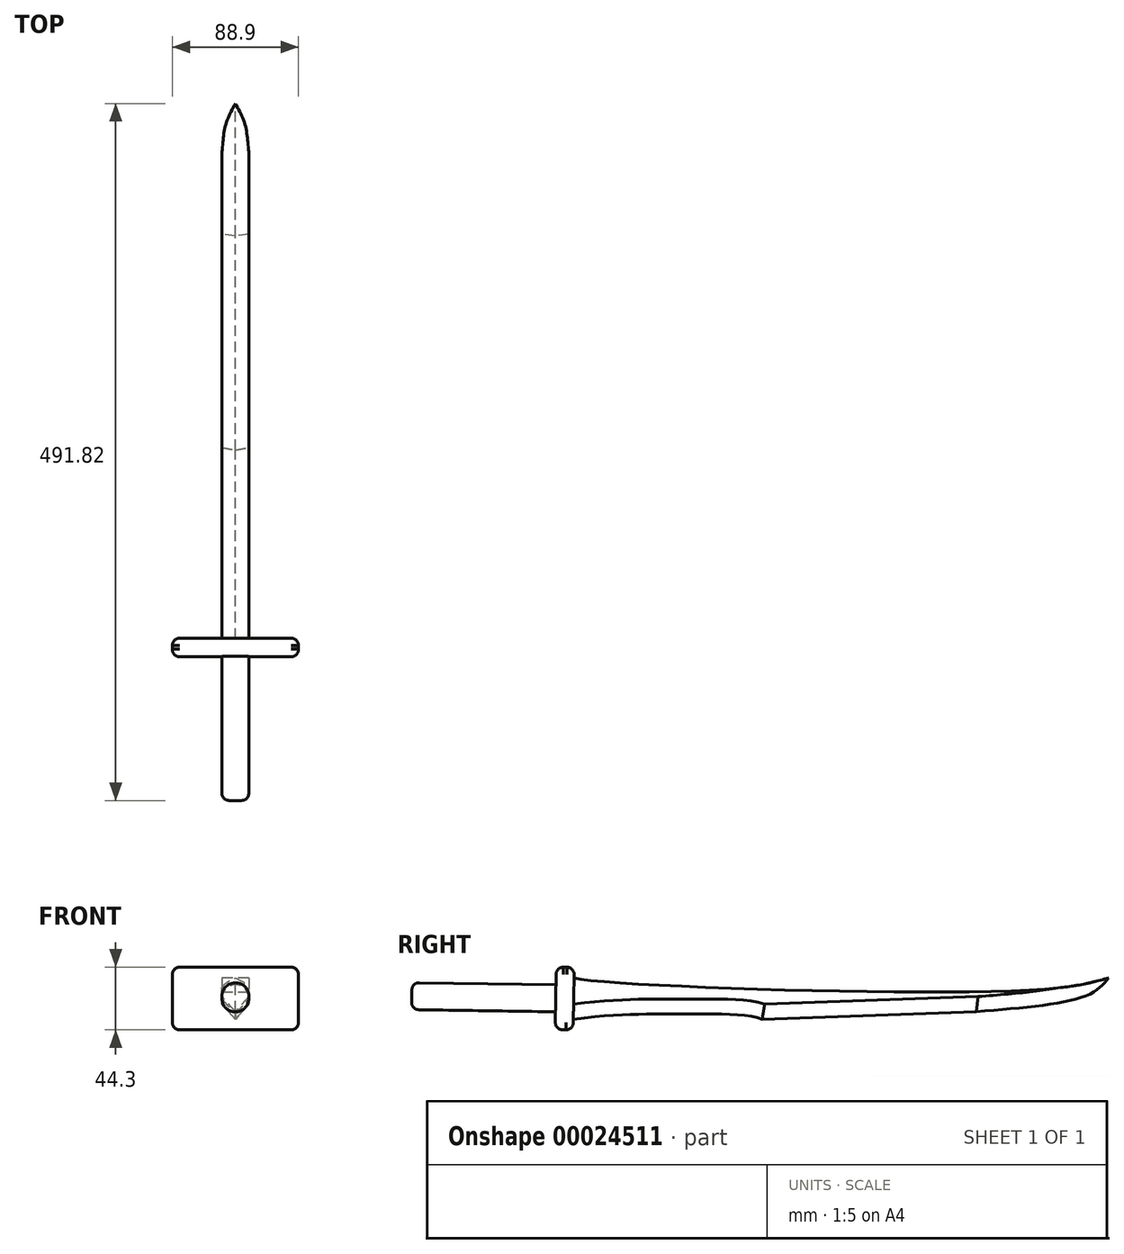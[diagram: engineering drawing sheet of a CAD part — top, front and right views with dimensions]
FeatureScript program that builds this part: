
annotation { "Feature Type Name" : "Feature", "Feature Type Description" : "" }
export const myFeature = defineFeature(function(context is Context, id is Id, definition is map)
    precondition{}
    {
        {
            var Q0;
            Q0=qCreatedBy(makeId("Right.planeOp"),FACE);
            var sketch = newSketch(context, id + "F0", { "sketchPlane" : qUnion([Q0])});
            skFitSpline(sketch, "E0", {"points": [v(0, 0) * mm, v(-14.62, -11.92) * mm, v(-93.35, -23.62) * mm], "startDerivative": vector(-32.8, -39.52) * mm, "endDerivative": vector(-141.4, -11) * mm});
            skLineSegment(sketch, "E1", {"start": v(-93.35, -23.62) * mm, "end": v(-244.5, -29.02) * mm});
            skFitSpline(sketch, "E2", {"points": [v(-244.5, -29.02) * mm, v(-301.66, -25.42) * mm, v(-377.69, -29.02) * mm], "startDerivative": vector(-70.94, 29.22) * mm, "endDerivative": vector(-184.3, -23.99) * mm});
            skFitSpline(sketch, "E3", {"points": [v(-377.24, 0) * mm, v(-52.88, -8.32) * mm, v(0, 0) * mm], "startDerivative": vector(106.12, -24.96) * mm, "endDerivative": vector(105.82, 24.98) * mm});
            skLineSegment(sketch, "E4", {"start": v(-377.24, 0) * mm, "end": v(-377.69, -29.02) * mm});
            skSolve(sketch);
        }
        {
            var Q0;
            Q0 = qSketchRegion(id + "F0", true);
            extrude(context, id + "F1", {"entities" : qUnion([Q0]), "depth" : 19.05 * mm});
        }
        {
            var Q0;
            Q0=makeQuery(id+"F1.opExtrude","SWEPT_FACE",FACE,{"disambiguationData":[OSD([sQuery(id+"F0.wireOp",EDGE,"E4")])]});
            var sketch = newSketch(context, id + "F2", { "sketchPlane" : qUnion([Q0])});
            skLineSegment(sketch, "E5", {"start": v(9.53, -34.87) * mm, "end": v(0, -24.2) * mm});
            skLineSegment(sketch, "E6", {"start": v(19.05, -24.2) * mm, "end": v(9.53, -34.87) * mm});
            skSolve(sketch);
        }
        {
            var Q0;
            {var subQ2=sQuery(id+"F2.wireOp",EDGE,"E5");Q0=makeQuery(id+"F2.imprint","IMPRINT",FACE,{"disambiguationData":[TD([[makeQuery(id+"F2.imprint","IMPRINT",EDGE,{"derivedFrom":subQ2}),1.0]])]});}
            var Q1;
            {var subQ2=sQuery(id+"F2.wireOp",EDGE,"E6");Q1=makeQuery(id+"F2.imprint","IMPRINT",FACE,{"disambiguationData":[TD([[makeQuery(id+"F2.imprint","IMPRINT",EDGE,{"derivedFrom":subQ2}),1.0]])]});}
            var Q2;
            Q2=makeQuery(id+"F1.opExtrude","CAP_EDGE",EDGE,{"disambiguationData":[OSD([sQuery(id+"F0.wireOp",EDGE,"E2")])],"isStart":false});
            var Q3;
            Q3=makeQuery(id+"F1.opExtrude","CAP_EDGE",EDGE,{"disambiguationData":[OSD([sQuery(id+"F0.wireOp",EDGE,"E1")])],"isStart":false});
            sweep(context, id + "F3", {"operationType" : NewBodyOperationType.REMOVE, "profiles" : qUnion([Q0, Q1]), "path" : qUnion([Q2, Q3])});
        }
        {
            var Q0;
            Q0=makeQuery(id+"F3.boolean.opBoolean","COPY",FACE,{"derivedFrom":makeQuery(id+"F3.opSweep","CAP_FACE",FACE,{"disambiguationData":[OSD([sQuery(id+"F0.wireOp",EDGE,"E0"),sQuery(id+"F0.wireOp",EDGE,"E1"),sQuery(id+"F0.wireOp",EDGE,"E2"),sQuery(id+"F0.wireOp",EDGE,"E4"),sQuery(id+"F2.wireOp",EDGE,"E6")])],"isStart":false})});
            var Q1;
            Q1=makeQuery(id+"F3.boolean.opBoolean","COPY",FACE,{"derivedFrom":makeQuery(id+"F3.opSweep","CAP_FACE",FACE,{"disambiguationData":[OSD([sQuery(id+"F0.wireOp",EDGE,"E0"),sQuery(id+"F0.wireOp",EDGE,"E1"),sQuery(id+"F0.wireOp",EDGE,"E2"),sQuery(id+"F0.wireOp",EDGE,"E4"),sQuery(id+"F2.wireOp",EDGE,"E5")])],"isStart":false})});
            var Q2;
            Q2=makeQuery(id+"F1.opExtrude","CAP_EDGE",EDGE,{"disambiguationData":[OSD([sQuery(id+"F0.wireOp",EDGE,"E0")])],"isStart":true});
            sweep(context, id + "F4", {"operationType" : NewBodyOperationType.REMOVE, "profiles" : qUnion([Q0, Q1]), "path" : qUnion([Q2])});
        }
        {
            var Q0;
            Q0=makeQuery(id+"F1.opExtrude","SWEPT_FACE",FACE,{"disambiguationData":[OSD([sQuery(id+"F0.wireOp",EDGE,"E4")])]});
            var sketch = newSketch(context, id + "F5", { "sketchPlane" : qUnion([Q0])});
            skLineSegment(sketch, "E7", {"start": v(9.53, -34.87) * mm, "end": v(28.58, -34.87) * mm});
            skLineSegment(sketch, "E8", {"start": v(9.53, -34.87) * mm, "end": v(-9.52, -34.87) * mm});
            skLineSegment(sketch, "E9", {"start": v(9.53, -5.85) * mm, "end": v(28.58, -5.85) * mm});
            skLineSegment(sketch, "E10", {"start": v(9.53, -5.85) * mm, "end": v(-9.52, -5.85) * mm});
            skLineSegment(sketch, "E11", {"start": v(-9.52, -5.85) * mm, "end": v(-9.52, -34.87) * mm});
            skLineSegment(sketch, "E12", {"start": v(28.58, -5.85) * mm, "end": v(28.58, -34.87) * mm});
            skSolve(sketch);
        }
        {
            var Q0;
            Q0 = qSketchRegion(id + "F5", true);
            extrude(context, id + "F6", {"entities" : qUnion([Q0]), "operationType" : NewBodyOperationType.ADD, "depth" : 12.7 * mm});
        }
        {
            var Q0;
            Q0=makeQuery(id+"F6.opExtrude","SWEPT_FACE",FACE,{"disambiguationData":[OSD([sQuery(id+"F5.wireOp",EDGE,"E11")])]});
            extrude(context, id + "F7", {"entities" : qUnion([Q0]), "operationType" : NewBodyOperationType.ADD, "depth" : 25.4 * mm});
        }
        {
            var Q0;
            Q0=makeQuery(id+"F6.opExtrude","SWEPT_FACE",FACE,{"disambiguationData":[OSD([sQuery(id+"F5.wireOp",EDGE,"E12")])]});
            extrude(context, id + "F8", {"entities" : qUnion([Q0]), "operationType" : NewBodyOperationType.ADD, "depth" : 25.4 * mm});
        }
        {
            var Q0;
            {var subQ0=sQuery(id+"F5.wireOp",EDGE,"E9");var subQ1=sQuery(id+"F5.wireOp",EDGE,"E10");Q0=makeQuery(id+"F8.boolean.opBoolean","MERGE",FACE,{"derivedFrom":[makeQuery(id+"F7.boolean.opBoolean","MERGE",FACE,{"derivedFrom":[makeQuery(id+"F6.opExtrude","SWEPT_FACE",FACE,{"disambiguationData":[OSD([subQ0,subQ1])]}),makeQuery(id+"F7.opExtrude","SWEPT_FACE",FACE,{"disambiguationData":[OSD([subQ1,sQuery(id+"F5.wireOp",EDGE,"E11")])]})]}),makeQuery(id+"F8.opExtrude","SWEPT_FACE",FACE,{"disambiguationData":[OSD([subQ0,sQuery(id+"F5.wireOp",EDGE,"E12")])]})]});}
            extrude(context, id + "F9", {"entities" : qUnion([Q0]), "operationType" : NewBodyOperationType.ADD, "depth" : 7.62 * mm});
        }
        {
            var Q0;
            {var subQ0=sQuery(id+"F5.wireOp",EDGE,"E7");var subQ1=sQuery(id+"F5.wireOp",EDGE,"E8");Q0=makeQuery(id+"F8.boolean.opBoolean","MERGE",FACE,{"derivedFrom":[makeQuery(id+"F7.boolean.opBoolean","MERGE",FACE,{"derivedFrom":[makeQuery(id+"F6.opExtrude","SWEPT_FACE",FACE,{"disambiguationData":[OSD([subQ0,subQ1])]}),makeQuery(id+"F7.opExtrude","SWEPT_FACE",FACE,{"disambiguationData":[OSD([subQ1,sQuery(id+"F5.wireOp",EDGE,"E11")])]})]}),makeQuery(id+"F8.opExtrude","SWEPT_FACE",FACE,{"disambiguationData":[OSD([subQ0,sQuery(id+"F5.wireOp",EDGE,"E12")])]})]});}
            extrude(context, id + "F10", {"entities" : qUnion([Q0]), "operationType" : NewBodyOperationType.ADD, "depth" : 7.62 * mm});
        }
        {
            var Q0;
            {var subQ0=sQuery(id+"F5.wireOp",EDGE,"E7");var subQ1=sQuery(id+"F5.wireOp",EDGE,"E8");var subQ2=sQuery(id+"F5.wireOp",EDGE,"E9");var subQ3=sQuery(id+"F5.wireOp",EDGE,"E10");var subQ4=sQuery(id+"F5.wireOp",EDGE,"E11");var subQ5=sQuery(id+"F5.wireOp",EDGE,"E12");Q0=makeQuery(id+"F10.boolean.opBoolean","MERGE",FACE,{"derivedFrom":[makeQuery(id+"F9.boolean.opBoolean","MERGE",FACE,{"derivedFrom":[makeQuery(id+"F8.boolean.opBoolean","MERGE",FACE,{"derivedFrom":[makeQuery(id+"F7.boolean.opBoolean","MERGE",FACE,{"derivedFrom":[makeQuery(id+"F6.opExtrude","CAP_FACE",FACE,{"disambiguationData":[OSD([subQ0,subQ1,subQ2,subQ3,subQ4,subQ5])],"isStart":false}),makeQuery(id+"F7.opExtrude","SWEPT_FACE",FACE,{"disambiguationData":[OSD([subQ4]),TDD([makeQuery(id+"F6.opExtrude","CAP_EDGE",EDGE,{"disambiguationData":[OSD([subQ4])],"isStart":false})])]})]}),makeQuery(id+"F8.opExtrude","SWEPT_FACE",FACE,{"disambiguationData":[OSD([subQ5]),TDD([makeQuery(id+"F6.opExtrude","CAP_EDGE",EDGE,{"disambiguationData":[OSD([subQ5])],"isStart":false})])]})]}),makeQuery(id+"F9.opExtrude","SWEPT_FACE",FACE,{"disambiguationData":[OSD([subQ2,subQ3,subQ4,subQ5])]})]}),makeQuery(id+"F10.opExtrude","SWEPT_FACE",FACE,{"disambiguationData":[OSD([subQ0,subQ1,subQ4,subQ5]),TDD([makeQuery(id+"F8.boolean.opBoolean","MERGE",EDGE,{"derivedFrom":[makeQuery(id+"F7.boolean.opBoolean","MERGE",EDGE,{"derivedFrom":[makeQuery(id+"F6.opExtrude","CAP_EDGE",EDGE,{"disambiguationData":[OSD([subQ0,subQ1])],"isStart":false}),makeQuery(id+"F7.opExtrude","SWEPT_EDGE",EDGE,{"disambiguationData":[OSD([subQ1,subQ4]),TDD([makeQuery(id+"F6.opExtrude","CAP_VERTEX",VERTEX,{"disambiguationData":[OSD([subQ1,subQ4])],"isStart":false})])]})]}),makeQuery(id+"F8.opExtrude","SWEPT_EDGE",EDGE,{"disambiguationData":[OSD([subQ0,subQ5]),TDD([makeQuery(id+"F6.opExtrude","CAP_VERTEX",VERTEX,{"disambiguationData":[OSD([subQ0,subQ5])],"isStart":false})])]})]})])]})]});}
            var sketch = newSketch(context, id + "F11", { "sketchPlane" : qUnion([Q0])});
            skCircle(sketch, "E13", {"center": v(9.53, -20.36) * mm, "radius": 9.53 * mm});
            skSolve(sketch);
        }
        {
            var Q0;
            Q0=makeQuery(id+"F9.opExtrude","CAP_EDGE",EDGE,{"disambiguationData":[OSD([sQuery(id+"F5.wireOp",EDGE,"E9"),sQuery(id+"F5.wireOp",EDGE,"E10"),sQuery(id+"F5.wireOp",EDGE,"E11"),sQuery(id+"F5.wireOp",EDGE,"E12")])],"isStart":false});
            var Q1;
            Q1=makeQuery(id+"F9.opExtrude","CAP_EDGE",EDGE,{"disambiguationData":[OSD([sQuery(id+"F0.wireOp",EDGE,"E3"),sQuery(id+"F0.wireOp",EDGE,"E4"),sQuery(id+"F5.wireOp",EDGE,"E9"),sQuery(id+"F5.wireOp",EDGE,"E10"),sQuery(id+"F5.wireOp",EDGE,"E11"),sQuery(id+"F5.wireOp",EDGE,"E12")])],"isStart":false});
            var Q2;
            {var subQ0=sQuery(id+"F5.wireOp",EDGE,"E11");var subQ1=sQuery(id+"F5.wireOp",EDGE,"E10");var subQ2=sQuery(id+"F5.wireOp",EDGE,"E8");Q2=makeQuery(id+"F10.boolean.opBoolean","MERGE",EDGE,{"derivedFrom":[makeQuery(id+"F9.boolean.opBoolean","MERGE",EDGE,{"derivedFrom":[makeQuery(id+"F7.opExtrude","CAP_EDGE",EDGE,{"disambiguationData":[OSD([subQ0]),TDD([makeQuery(id+"F6.opExtrude","CAP_EDGE",EDGE,{"disambiguationData":[OSD([subQ0])],"isStart":true})])],"isStart":false}),makeQuery(id+"F9.opExtrude","SWEPT_EDGE",EDGE,{"disambiguationData":[OSD([subQ1,subQ0]),TDD([makeQuery(id+"F7.opExtrude","CAP_VERTEX",VERTEX,{"disambiguationData":[OSD([subQ1,subQ0]),TDD([makeQuery(id+"F6.opExtrude","CAP_VERTEX",VERTEX,{"disambiguationData":[OSD([subQ1,subQ0])],"isStart":true})])],"isStart":false})])]})]}),makeQuery(id+"F10.opExtrude","SWEPT_EDGE",EDGE,{"disambiguationData":[OSD([subQ2,subQ0]),TDD([makeQuery(id+"F7.opExtrude","CAP_VERTEX",VERTEX,{"disambiguationData":[OSD([subQ2,subQ0]),TDD([makeQuery(id+"F6.opExtrude","CAP_VERTEX",VERTEX,{"disambiguationData":[OSD([subQ2,subQ0])],"isStart":true})])],"isStart":false})])]})]});}
            var Q3;
            {var subQ0=sQuery(id+"F5.wireOp",EDGE,"E11");var subQ1=sQuery(id+"F5.wireOp",EDGE,"E10");var subQ2=sQuery(id+"F5.wireOp",EDGE,"E8");Q3=makeQuery(id+"F10.boolean.opBoolean","MERGE",EDGE,{"derivedFrom":[makeQuery(id+"F9.boolean.opBoolean","MERGE",EDGE,{"derivedFrom":[makeQuery(id+"F7.opExtrude","CAP_EDGE",EDGE,{"disambiguationData":[OSD([subQ0]),TDD([makeQuery(id+"F6.opExtrude","CAP_EDGE",EDGE,{"disambiguationData":[OSD([subQ0])],"isStart":false})])],"isStart":false}),makeQuery(id+"F9.opExtrude","SWEPT_EDGE",EDGE,{"disambiguationData":[OSD([subQ1,subQ0]),TDD([makeQuery(id+"F7.opExtrude","CAP_VERTEX",VERTEX,{"disambiguationData":[OSD([subQ1,subQ0]),TDD([makeQuery(id+"F6.opExtrude","CAP_VERTEX",VERTEX,{"disambiguationData":[OSD([subQ1,subQ0])],"isStart":false})])],"isStart":false})])]})]}),makeQuery(id+"F10.opExtrude","SWEPT_EDGE",EDGE,{"disambiguationData":[OSD([subQ2,subQ0]),TDD([makeQuery(id+"F7.opExtrude","CAP_VERTEX",VERTEX,{"disambiguationData":[OSD([subQ2,subQ0]),TDD([makeQuery(id+"F6.opExtrude","CAP_VERTEX",VERTEX,{"disambiguationData":[OSD([subQ2,subQ0])],"isStart":false})])],"isStart":false})])]})]});}
            var Q4;
            {var subQ0=sQuery(id+"F5.wireOp",EDGE,"E7");var subQ1=sQuery(id+"F5.wireOp",EDGE,"E8");var subQ2=sQuery(id+"F5.wireOp",EDGE,"E11");var subQ3=sQuery(id+"F5.wireOp",EDGE,"E12");var subQ4=makeQuery(id+"F6.opExtrude","CAP_EDGE",EDGE,{"disambiguationData":[OSD([subQ0,subQ1])],"isStart":true});Q4=makeQuery(id+"F10.opExtrude","CAP_EDGE",EDGE,{"disambiguationData":[OSD([subQ0,subQ1,subQ2,subQ3]),TDD([makeQuery(id+"F7.boolean.opBoolean","MERGE",EDGE,{"derivedFrom":[makeQuery(id+"F6.boolean.opBoolean","SPLIT",EDGE,{"disambiguationData":[TD([makeQuery(id+"F6.opExtrude","SWEPT_FACE",FACE,{"disambiguationData":[OSD([subQ2])]})])],"derivedFrom":subQ4}),makeQuery(id+"F7.opExtrude","SWEPT_EDGE",EDGE,{"disambiguationData":[OSD([subQ1,subQ2]),TDD([makeQuery(id+"F6.opExtrude","CAP_VERTEX",VERTEX,{"disambiguationData":[OSD([subQ1,subQ2])],"isStart":true})])]})]}),makeQuery(id+"F8.boolean.opBoolean","MERGE",EDGE,{"derivedFrom":[makeQuery(id+"F6.boolean.opBoolean","SPLIT",EDGE,{"disambiguationData":[TD([makeQuery(id+"F6.opExtrude","SWEPT_FACE",FACE,{"disambiguationData":[OSD([subQ3])]})])],"derivedFrom":subQ4}),makeQuery(id+"F8.opExtrude","SWEPT_EDGE",EDGE,{"disambiguationData":[OSD([subQ0,subQ3]),TDD([makeQuery(id+"F6.opExtrude","CAP_VERTEX",VERTEX,{"disambiguationData":[OSD([subQ0,subQ3])],"isStart":true})])]})]})])],"isStart":false});}
            var Q5;
            {var subQ0=sQuery(id+"F5.wireOp",EDGE,"E12");var subQ1=sQuery(id+"F5.wireOp",EDGE,"E9");var subQ2=sQuery(id+"F5.wireOp",EDGE,"E7");Q5=makeQuery(id+"F10.boolean.opBoolean","MERGE",EDGE,{"derivedFrom":[makeQuery(id+"F9.boolean.opBoolean","MERGE",EDGE,{"derivedFrom":[makeQuery(id+"F8.opExtrude","CAP_EDGE",EDGE,{"disambiguationData":[OSD([subQ0]),TDD([makeQuery(id+"F6.opExtrude","CAP_EDGE",EDGE,{"disambiguationData":[OSD([subQ0])],"isStart":false})])],"isStart":false}),makeQuery(id+"F9.opExtrude","SWEPT_EDGE",EDGE,{"disambiguationData":[OSD([subQ1,subQ0]),TDD([makeQuery(id+"F8.opExtrude","CAP_VERTEX",VERTEX,{"disambiguationData":[OSD([subQ1,subQ0]),TDD([makeQuery(id+"F6.opExtrude","CAP_VERTEX",VERTEX,{"disambiguationData":[OSD([subQ1,subQ0])],"isStart":false})])],"isStart":false})])]})]}),makeQuery(id+"F10.opExtrude","SWEPT_EDGE",EDGE,{"disambiguationData":[OSD([subQ2,subQ0]),TDD([makeQuery(id+"F8.opExtrude","CAP_VERTEX",VERTEX,{"disambiguationData":[OSD([subQ2,subQ0]),TDD([makeQuery(id+"F6.opExtrude","CAP_VERTEX",VERTEX,{"disambiguationData":[OSD([subQ2,subQ0])],"isStart":false})])],"isStart":false})])]})]});}
            var Q6;
            {var subQ0=sQuery(id+"F5.wireOp",EDGE,"E12");var subQ1=sQuery(id+"F5.wireOp",EDGE,"E9");var subQ2=sQuery(id+"F5.wireOp",EDGE,"E7");Q6=makeQuery(id+"F10.boolean.opBoolean","MERGE",EDGE,{"derivedFrom":[makeQuery(id+"F9.boolean.opBoolean","MERGE",EDGE,{"derivedFrom":[makeQuery(id+"F8.opExtrude","CAP_EDGE",EDGE,{"disambiguationData":[OSD([subQ0]),TDD([makeQuery(id+"F6.opExtrude","CAP_EDGE",EDGE,{"disambiguationData":[OSD([subQ0])],"isStart":true})])],"isStart":false}),makeQuery(id+"F9.opExtrude","SWEPT_EDGE",EDGE,{"disambiguationData":[OSD([subQ1,subQ0]),TDD([makeQuery(id+"F8.opExtrude","CAP_VERTEX",VERTEX,{"disambiguationData":[OSD([subQ1,subQ0]),TDD([makeQuery(id+"F6.opExtrude","CAP_VERTEX",VERTEX,{"disambiguationData":[OSD([subQ1,subQ0])],"isStart":true})])],"isStart":false})])]})]}),makeQuery(id+"F10.opExtrude","SWEPT_EDGE",EDGE,{"disambiguationData":[OSD([subQ2,subQ0]),TDD([makeQuery(id+"F8.opExtrude","CAP_VERTEX",VERTEX,{"disambiguationData":[OSD([subQ2,subQ0]),TDD([makeQuery(id+"F6.opExtrude","CAP_VERTEX",VERTEX,{"disambiguationData":[OSD([subQ2,subQ0])],"isStart":true})])],"isStart":false})])]})]});}
            fillet(context, id + "F12", {"entities" : qUnion([Q0, Q1, Q2, Q3, Q4, Q5, Q6]), "radius" : 5.08 * mm, "tangentPropagation" : true, "allowEdgeOverflow" : false});
        }
        {
            var Q0;
            Q0 = qSketchRegion(id + "F11", true);
            extrude(context, id + "F13", {"entities" : qUnion([Q0]), "operationType" : NewBodyOperationType.ADD, "depth" : 101.6 * mm});
        }
        {
            var Q0;
            Q0=makeQuery(id+"F13.opExtrude","CAP_EDGE",EDGE,{"disambiguationData":[OSD([sQuery(id+"F11.wireOp",EDGE,"E13")])],"isStart":false});
            fillet(context, id + "F14", {"entities" : qUnion([Q0]), "radius" : 5.08 * mm, "tangentPropagation" : true, "allowEdgeOverflow" : false});
        }
        {
            var Q0;
            {var subQ0=sQuery(id+"F5.wireOp",EDGE,"E9");var subQ1=sQuery(id+"F5.wireOp",EDGE,"E12");var subQ2=sQuery(id+"F5.wireOp",EDGE,"E7");Q0=makeQuery(id+"F12.opFillet","BLEND_EDGE",EDGE,{"blendedFrom":[makeQuery(id+"F9.opExtrude","CAP_EDGE",EDGE,{"disambiguationData":[OSD([sQuery(id+"F0.wireOp",EDGE,"E3"),sQuery(id+"F0.wireOp",EDGE,"E4"),subQ0,sQuery(id+"F5.wireOp",EDGE,"E10"),sQuery(id+"F5.wireOp",EDGE,"E11"),subQ1])],"isStart":false}),makeQuery(id+"F10.boolean.opBoolean","MERGE",EDGE,{"derivedFrom":[makeQuery(id+"F9.boolean.opBoolean","MERGE",EDGE,{"derivedFrom":[makeQuery(id+"F8.opExtrude","CAP_EDGE",EDGE,{"disambiguationData":[OSD([subQ1]),TDD([makeQuery(id+"F6.opExtrude","CAP_EDGE",EDGE,{"disambiguationData":[OSD([subQ1])],"isStart":true})])],"isStart":false}),makeQuery(id+"F9.opExtrude","SWEPT_EDGE",EDGE,{"disambiguationData":[OSD([subQ0,subQ1]),TDD([makeQuery(id+"F8.opExtrude","CAP_VERTEX",VERTEX,{"disambiguationData":[OSD([subQ0,subQ1]),TDD([makeQuery(id+"F6.opExtrude","CAP_VERTEX",VERTEX,{"disambiguationData":[OSD([subQ0,subQ1])],"isStart":true})])],"isStart":false})])]})]}),makeQuery(id+"F10.opExtrude","SWEPT_EDGE",EDGE,{"disambiguationData":[OSD([subQ2,subQ1]),TDD([makeQuery(id+"F8.opExtrude","CAP_VERTEX",VERTEX,{"disambiguationData":[OSD([subQ2,subQ1]),TDD([makeQuery(id+"F6.opExtrude","CAP_VERTEX",VERTEX,{"disambiguationData":[OSD([subQ2,subQ1])],"isStart":true})])],"isStart":false})])]})]})],"blendedInto":[]});}
            var Q1;
            {var subQ0=sQuery(id+"F5.wireOp",EDGE,"E10");var subQ1=sQuery(id+"F5.wireOp",EDGE,"E11");var subQ2=sQuery(id+"F5.wireOp",EDGE,"E8");Q1=makeQuery(id+"F12.opFillet","BLEND_EDGE",EDGE,{"blendedFrom":[makeQuery(id+"F9.opExtrude","CAP_EDGE",EDGE,{"disambiguationData":[OSD([sQuery(id+"F0.wireOp",EDGE,"E3"),sQuery(id+"F0.wireOp",EDGE,"E4"),sQuery(id+"F5.wireOp",EDGE,"E9"),subQ0,subQ1,sQuery(id+"F5.wireOp",EDGE,"E12")])],"isStart":false}),makeQuery(id+"F10.boolean.opBoolean","MERGE",EDGE,{"derivedFrom":[makeQuery(id+"F9.boolean.opBoolean","MERGE",EDGE,{"derivedFrom":[makeQuery(id+"F7.opExtrude","CAP_EDGE",EDGE,{"disambiguationData":[OSD([subQ1]),TDD([makeQuery(id+"F6.opExtrude","CAP_EDGE",EDGE,{"disambiguationData":[OSD([subQ1])],"isStart":true})])],"isStart":false}),makeQuery(id+"F9.opExtrude","SWEPT_EDGE",EDGE,{"disambiguationData":[OSD([subQ0,subQ1]),TDD([makeQuery(id+"F7.opExtrude","CAP_VERTEX",VERTEX,{"disambiguationData":[OSD([subQ0,subQ1]),TDD([makeQuery(id+"F6.opExtrude","CAP_VERTEX",VERTEX,{"disambiguationData":[OSD([subQ0,subQ1])],"isStart":true})])],"isStart":false})])]})]}),makeQuery(id+"F10.opExtrude","SWEPT_EDGE",EDGE,{"disambiguationData":[OSD([subQ2,subQ1]),TDD([makeQuery(id+"F7.opExtrude","CAP_VERTEX",VERTEX,{"disambiguationData":[OSD([subQ2,subQ1]),TDD([makeQuery(id+"F6.opExtrude","CAP_VERTEX",VERTEX,{"disambiguationData":[OSD([subQ2,subQ1])],"isStart":true})])],"isStart":false})])]})]})],"blendedInto":[]});}
            var Q2;
            {var subQ0=sQuery(id+"F5.wireOp",EDGE,"E7");var subQ1=sQuery(id+"F5.wireOp",EDGE,"E8");var subQ2=sQuery(id+"F5.wireOp",EDGE,"E11");var subQ3=sQuery(id+"F5.wireOp",EDGE,"E12");var subQ4=makeQuery(id+"F6.opExtrude","CAP_EDGE",EDGE,{"disambiguationData":[OSD([subQ0,subQ1])],"isStart":true});var subQ5=sQuery(id+"F5.wireOp",EDGE,"E9");var subQ11=makeQuery(id+"F6.opExtrude","CAP_VERTEX",VERTEX,{"disambiguationData":[OSD([subQ0,subQ3])],"isStart":true});Q2=makeQuery(id+"F12.opFillet","BLEND_EDGE",EDGE,{"blendedFrom":[makeQuery(id+"F10.opExtrude","CAP_EDGE",EDGE,{"disambiguationData":[OSD([subQ0,subQ1,subQ2,subQ3]),TDD([makeQuery(id+"F7.boolean.opBoolean","MERGE",EDGE,{"derivedFrom":[makeQuery(id+"F6.boolean.opBoolean","SPLIT",EDGE,{"disambiguationData":[TD([makeQuery(id+"F6.opExtrude","SWEPT_FACE",FACE,{"disambiguationData":[OSD([subQ2])]})])],"derivedFrom":subQ4}),makeQuery(id+"F7.opExtrude","SWEPT_EDGE",EDGE,{"disambiguationData":[OSD([subQ1,subQ2]),TDD([makeQuery(id+"F6.opExtrude","CAP_VERTEX",VERTEX,{"disambiguationData":[OSD([subQ1,subQ2])],"isStart":true})])]})]}),makeQuery(id+"F8.boolean.opBoolean","MERGE",EDGE,{"derivedFrom":[makeQuery(id+"F6.boolean.opBoolean","SPLIT",EDGE,{"disambiguationData":[TD([makeQuery(id+"F6.opExtrude","SWEPT_FACE",FACE,{"disambiguationData":[OSD([subQ3])]})])],"derivedFrom":subQ4}),makeQuery(id+"F8.opExtrude","SWEPT_EDGE",EDGE,{"disambiguationData":[OSD([subQ0,subQ3]),TDD([subQ11])]})]})])],"isStart":false}),makeQuery(id+"F10.boolean.opBoolean","MERGE",EDGE,{"derivedFrom":[makeQuery(id+"F9.boolean.opBoolean","MERGE",EDGE,{"derivedFrom":[makeQuery(id+"F8.opExtrude","CAP_EDGE",EDGE,{"disambiguationData":[OSD([subQ3]),TDD([makeQuery(id+"F6.opExtrude","CAP_EDGE",EDGE,{"disambiguationData":[OSD([subQ3])],"isStart":true})])],"isStart":false}),makeQuery(id+"F9.opExtrude","SWEPT_EDGE",EDGE,{"disambiguationData":[OSD([subQ5,subQ3]),TDD([makeQuery(id+"F8.opExtrude","CAP_VERTEX",VERTEX,{"disambiguationData":[OSD([subQ5,subQ3]),TDD([makeQuery(id+"F6.opExtrude","CAP_VERTEX",VERTEX,{"disambiguationData":[OSD([subQ5,subQ3])],"isStart":true})])],"isStart":false})])]})]}),makeQuery(id+"F10.opExtrude","SWEPT_EDGE",EDGE,{"disambiguationData":[OSD([subQ0,subQ3]),TDD([makeQuery(id+"F8.opExtrude","CAP_VERTEX",VERTEX,{"disambiguationData":[OSD([subQ0,subQ3]),TDD([subQ11])],"isStart":false})])]})]})],"blendedInto":[]});}
            var Q3;
            {var subQ0=sQuery(id+"F5.wireOp",EDGE,"E7");var subQ1=sQuery(id+"F5.wireOp",EDGE,"E8");var subQ2=sQuery(id+"F5.wireOp",EDGE,"E11");var subQ3=sQuery(id+"F5.wireOp",EDGE,"E12");var subQ4=makeQuery(id+"F6.opExtrude","CAP_EDGE",EDGE,{"disambiguationData":[OSD([subQ0,subQ1])],"isStart":true});var subQ5=sQuery(id+"F5.wireOp",EDGE,"E10");var subQ11=makeQuery(id+"F6.opExtrude","CAP_VERTEX",VERTEX,{"disambiguationData":[OSD([subQ1,subQ2])],"isStart":true});Q3=makeQuery(id+"F12.opFillet","BLEND_EDGE",EDGE,{"blendedFrom":[makeQuery(id+"F10.opExtrude","CAP_EDGE",EDGE,{"disambiguationData":[OSD([subQ0,subQ1,subQ2,subQ3]),TDD([makeQuery(id+"F7.boolean.opBoolean","MERGE",EDGE,{"derivedFrom":[makeQuery(id+"F6.boolean.opBoolean","SPLIT",EDGE,{"disambiguationData":[TD([makeQuery(id+"F6.opExtrude","SWEPT_FACE",FACE,{"disambiguationData":[OSD([subQ2])]})])],"derivedFrom":subQ4}),makeQuery(id+"F7.opExtrude","SWEPT_EDGE",EDGE,{"disambiguationData":[OSD([subQ1,subQ2]),TDD([subQ11])]})]}),makeQuery(id+"F8.boolean.opBoolean","MERGE",EDGE,{"derivedFrom":[makeQuery(id+"F6.boolean.opBoolean","SPLIT",EDGE,{"disambiguationData":[TD([makeQuery(id+"F6.opExtrude","SWEPT_FACE",FACE,{"disambiguationData":[OSD([subQ3])]})])],"derivedFrom":subQ4}),makeQuery(id+"F8.opExtrude","SWEPT_EDGE",EDGE,{"disambiguationData":[OSD([subQ0,subQ3]),TDD([makeQuery(id+"F6.opExtrude","CAP_VERTEX",VERTEX,{"disambiguationData":[OSD([subQ0,subQ3])],"isStart":true})])]})]})])],"isStart":false}),makeQuery(id+"F10.boolean.opBoolean","MERGE",EDGE,{"derivedFrom":[makeQuery(id+"F9.boolean.opBoolean","MERGE",EDGE,{"derivedFrom":[makeQuery(id+"F7.opExtrude","CAP_EDGE",EDGE,{"disambiguationData":[OSD([subQ2]),TDD([makeQuery(id+"F6.opExtrude","CAP_EDGE",EDGE,{"disambiguationData":[OSD([subQ2])],"isStart":true})])],"isStart":false}),makeQuery(id+"F9.opExtrude","SWEPT_EDGE",EDGE,{"disambiguationData":[OSD([subQ5,subQ2]),TDD([makeQuery(id+"F7.opExtrude","CAP_VERTEX",VERTEX,{"disambiguationData":[OSD([subQ5,subQ2]),TDD([makeQuery(id+"F6.opExtrude","CAP_VERTEX",VERTEX,{"disambiguationData":[OSD([subQ5,subQ2])],"isStart":true})])],"isStart":false})])]})]}),makeQuery(id+"F10.opExtrude","SWEPT_EDGE",EDGE,{"disambiguationData":[OSD([subQ1,subQ2]),TDD([makeQuery(id+"F7.opExtrude","CAP_VERTEX",VERTEX,{"disambiguationData":[OSD([subQ1,subQ2]),TDD([subQ11])],"isStart":false})])]})]})],"blendedInto":[]});}
            var Q4;
            {var subQ0=sQuery(id+"F5.wireOp",EDGE,"E9");var subQ1=sQuery(id+"F5.wireOp",EDGE,"E12");var subQ2=sQuery(id+"F5.wireOp",EDGE,"E7");Q4=makeQuery(id+"F12.opFillet","BLEND_EDGE",EDGE,{"blendedFrom":[makeQuery(id+"F9.opExtrude","CAP_EDGE",EDGE,{"disambiguationData":[OSD([subQ0,sQuery(id+"F5.wireOp",EDGE,"E10"),sQuery(id+"F5.wireOp",EDGE,"E11"),subQ1])],"isStart":false}),makeQuery(id+"F10.boolean.opBoolean","MERGE",EDGE,{"derivedFrom":[makeQuery(id+"F9.boolean.opBoolean","MERGE",EDGE,{"derivedFrom":[makeQuery(id+"F8.opExtrude","CAP_EDGE",EDGE,{"disambiguationData":[OSD([subQ1]),TDD([makeQuery(id+"F6.opExtrude","CAP_EDGE",EDGE,{"disambiguationData":[OSD([subQ1])],"isStart":false})])],"isStart":false}),makeQuery(id+"F9.opExtrude","SWEPT_EDGE",EDGE,{"disambiguationData":[OSD([subQ0,subQ1]),TDD([makeQuery(id+"F8.opExtrude","CAP_VERTEX",VERTEX,{"disambiguationData":[OSD([subQ0,subQ1]),TDD([makeQuery(id+"F6.opExtrude","CAP_VERTEX",VERTEX,{"disambiguationData":[OSD([subQ0,subQ1])],"isStart":false})])],"isStart":false})])]})]}),makeQuery(id+"F10.opExtrude","SWEPT_EDGE",EDGE,{"disambiguationData":[OSD([subQ2,subQ1]),TDD([makeQuery(id+"F8.opExtrude","CAP_VERTEX",VERTEX,{"disambiguationData":[OSD([subQ2,subQ1]),TDD([makeQuery(id+"F6.opExtrude","CAP_VERTEX",VERTEX,{"disambiguationData":[OSD([subQ2,subQ1])],"isStart":false})])],"isStart":false})])]})]})],"blendedInto":[]});}
            var Q5;
            {var subQ0=sQuery(id+"F5.wireOp",EDGE,"E12");var subQ1=sQuery(id+"F5.wireOp",EDGE,"E9");var subQ2=sQuery(id+"F5.wireOp",EDGE,"E7");Q5=makeQuery(id+"F12.opFillet","BLEND_EDGE",EDGE,{"blendedFrom":[makeQuery(id+"F10.boolean.opBoolean","MERGE",EDGE,{"derivedFrom":[makeQuery(id+"F9.boolean.opBoolean","MERGE",EDGE,{"derivedFrom":[makeQuery(id+"F8.opExtrude","CAP_EDGE",EDGE,{"disambiguationData":[OSD([subQ0]),TDD([makeQuery(id+"F6.opExtrude","CAP_EDGE",EDGE,{"disambiguationData":[OSD([subQ0])],"isStart":false})])],"isStart":false}),makeQuery(id+"F9.opExtrude","SWEPT_EDGE",EDGE,{"disambiguationData":[OSD([subQ1,subQ0]),TDD([makeQuery(id+"F8.opExtrude","CAP_VERTEX",VERTEX,{"disambiguationData":[OSD([subQ1,subQ0]),TDD([makeQuery(id+"F6.opExtrude","CAP_VERTEX",VERTEX,{"disambiguationData":[OSD([subQ1,subQ0])],"isStart":false})])],"isStart":false})])]})]}),makeQuery(id+"F10.opExtrude","SWEPT_EDGE",EDGE,{"disambiguationData":[OSD([subQ2,subQ0]),TDD([makeQuery(id+"F8.opExtrude","CAP_VERTEX",VERTEX,{"disambiguationData":[OSD([subQ2,subQ0]),TDD([makeQuery(id+"F6.opExtrude","CAP_VERTEX",VERTEX,{"disambiguationData":[OSD([subQ2,subQ0])],"isStart":false})])],"isStart":false})])]})]}),makeQuery(id+"F10.opExtrude","CAP_FACE",FACE,{"disambiguationData":[OSD([subQ2,sQuery(id+"F5.wireOp",EDGE,"E8"),sQuery(id+"F5.wireOp",EDGE,"E11"),subQ0])],"isStart":false})],"blendedInto":[makeQuery(id+"F10.opExtrude","CAP_FACE",FACE,{"disambiguationData":[OSD([subQ2,sQuery(id+"F5.wireOp",EDGE,"E8"),sQuery(id+"F5.wireOp",EDGE,"E11"),subQ0])],"isStart":false})]});}
            var Q6;
            {var subQ0=sQuery(id+"F5.wireOp",EDGE,"E12");var subQ1=sQuery(id+"F5.wireOp",EDGE,"E9");var subQ2=sQuery(id+"F5.wireOp",EDGE,"E7");Q6=makeQuery(id+"F12.opFillet","BLEND_EDGE",EDGE,{"blendedFrom":[makeQuery(id+"F10.boolean.opBoolean","MERGE",EDGE,{"derivedFrom":[makeQuery(id+"F9.boolean.opBoolean","MERGE",EDGE,{"derivedFrom":[makeQuery(id+"F8.opExtrude","CAP_EDGE",EDGE,{"disambiguationData":[OSD([subQ0]),TDD([makeQuery(id+"F6.opExtrude","CAP_EDGE",EDGE,{"disambiguationData":[OSD([subQ0])],"isStart":false})])],"isStart":false}),makeQuery(id+"F9.opExtrude","SWEPT_EDGE",EDGE,{"disambiguationData":[OSD([subQ1,subQ0]),TDD([makeQuery(id+"F8.opExtrude","CAP_VERTEX",VERTEX,{"disambiguationData":[OSD([subQ1,subQ0]),TDD([makeQuery(id+"F6.opExtrude","CAP_VERTEX",VERTEX,{"disambiguationData":[OSD([subQ1,subQ0])],"isStart":false})])],"isStart":false})])]})]}),makeQuery(id+"F10.opExtrude","SWEPT_EDGE",EDGE,{"disambiguationData":[OSD([subQ2,subQ0]),TDD([makeQuery(id+"F8.opExtrude","CAP_VERTEX",VERTEX,{"disambiguationData":[OSD([subQ2,subQ0]),TDD([makeQuery(id+"F6.opExtrude","CAP_VERTEX",VERTEX,{"disambiguationData":[OSD([subQ2,subQ0])],"isStart":false})])],"isStart":false})])]})]}),makeQuery(id+"F10.boolean.opBoolean","MERGE",FACE,{"derivedFrom":[makeQuery(id+"F9.boolean.opBoolean","MERGE",FACE,{"derivedFrom":[makeQuery(id+"F8.opExtrude","CAP_FACE",FACE,{"disambiguationData":[OSD([subQ0])],"isStart":false}),makeQuery(id+"F9.opExtrude","SWEPT_FACE",FACE,{"disambiguationData":[OSD([subQ1,subQ0])]})]}),makeQuery(id+"F10.opExtrude","SWEPT_FACE",FACE,{"disambiguationData":[OSD([subQ2,subQ0])]})]})],"blendedInto":[makeQuery(id+"F10.boolean.opBoolean","MERGE",FACE,{"derivedFrom":[makeQuery(id+"F9.boolean.opBoolean","MERGE",FACE,{"derivedFrom":[makeQuery(id+"F8.opExtrude","CAP_FACE",FACE,{"disambiguationData":[OSD([subQ0])],"isStart":false}),makeQuery(id+"F9.opExtrude","SWEPT_FACE",FACE,{"disambiguationData":[OSD([subQ1,subQ0])]})]}),makeQuery(id+"F10.opExtrude","SWEPT_FACE",FACE,{"disambiguationData":[OSD([subQ2,subQ0])]})]})]});}
            var Q7;
            {var subQ0=sQuery(id+"F5.wireOp",EDGE,"E12");var subQ1=sQuery(id+"F5.wireOp",EDGE,"E9");var subQ2=sQuery(id+"F5.wireOp",EDGE,"E7");Q7=makeQuery(id+"F12.opFillet","BLEND_EDGE",EDGE,{"blendedFrom":[makeQuery(id+"F10.boolean.opBoolean","MERGE",EDGE,{"derivedFrom":[makeQuery(id+"F9.boolean.opBoolean","MERGE",EDGE,{"derivedFrom":[makeQuery(id+"F8.opExtrude","CAP_EDGE",EDGE,{"disambiguationData":[OSD([subQ0]),TDD([makeQuery(id+"F6.opExtrude","CAP_EDGE",EDGE,{"disambiguationData":[OSD([subQ0])],"isStart":true})])],"isStart":false}),makeQuery(id+"F9.opExtrude","SWEPT_EDGE",EDGE,{"disambiguationData":[OSD([subQ1,subQ0]),TDD([makeQuery(id+"F8.opExtrude","CAP_VERTEX",VERTEX,{"disambiguationData":[OSD([subQ1,subQ0]),TDD([makeQuery(id+"F6.opExtrude","CAP_VERTEX",VERTEX,{"disambiguationData":[OSD([subQ1,subQ0])],"isStart":true})])],"isStart":false})])]})]}),makeQuery(id+"F10.opExtrude","SWEPT_EDGE",EDGE,{"disambiguationData":[OSD([subQ2,subQ0]),TDD([makeQuery(id+"F8.opExtrude","CAP_VERTEX",VERTEX,{"disambiguationData":[OSD([subQ2,subQ0]),TDD([makeQuery(id+"F6.opExtrude","CAP_VERTEX",VERTEX,{"disambiguationData":[OSD([subQ2,subQ0])],"isStart":true})])],"isStart":false})])]})]}),makeQuery(id+"F10.boolean.opBoolean","MERGE",FACE,{"derivedFrom":[makeQuery(id+"F9.boolean.opBoolean","MERGE",FACE,{"derivedFrom":[makeQuery(id+"F8.opExtrude","CAP_FACE",FACE,{"disambiguationData":[OSD([subQ0])],"isStart":false}),makeQuery(id+"F9.opExtrude","SWEPT_FACE",FACE,{"disambiguationData":[OSD([subQ1,subQ0])]})]}),makeQuery(id+"F10.opExtrude","SWEPT_FACE",FACE,{"disambiguationData":[OSD([subQ2,subQ0])]})]})],"blendedInto":[makeQuery(id+"F10.boolean.opBoolean","MERGE",FACE,{"derivedFrom":[makeQuery(id+"F9.boolean.opBoolean","MERGE",FACE,{"derivedFrom":[makeQuery(id+"F8.opExtrude","CAP_FACE",FACE,{"disambiguationData":[OSD([subQ0])],"isStart":false}),makeQuery(id+"F9.opExtrude","SWEPT_FACE",FACE,{"disambiguationData":[OSD([subQ1,subQ0])]})]}),makeQuery(id+"F10.opExtrude","SWEPT_FACE",FACE,{"disambiguationData":[OSD([subQ2,subQ0])]})]})]});}
            var Q8;
            {var subQ0=sQuery(id+"F5.wireOp",EDGE,"E12");Q8=makeQuery(id+"F10.boolean.opBoolean","MERGE",FACE,{"derivedFrom":[makeQuery(id+"F9.boolean.opBoolean","MERGE",FACE,{"derivedFrom":[makeQuery(id+"F8.opExtrude","CAP_FACE",FACE,{"disambiguationData":[OSD([subQ0])],"isStart":false}),makeQuery(id+"F9.opExtrude","SWEPT_FACE",FACE,{"disambiguationData":[OSD([sQuery(id+"F5.wireOp",EDGE,"E9"),subQ0])]})]}),makeQuery(id+"F10.opExtrude","SWEPT_FACE",FACE,{"disambiguationData":[OSD([sQuery(id+"F5.wireOp",EDGE,"E7"),subQ0])]})]});}
            fillet(context, id + "F15", {"entities" : qUnion([Q0, Q1, Q2, Q3, Q4, Q5, Q6, Q7, Q8]), "radius" : 5.08 * mm, "tangentPropagation" : true, "allowEdgeOverflow" : false});
        }
    });
